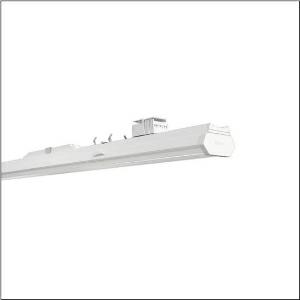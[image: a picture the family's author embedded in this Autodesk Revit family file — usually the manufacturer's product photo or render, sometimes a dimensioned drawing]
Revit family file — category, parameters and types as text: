
# Revit family: licross_r__11_protected_ho_51td11cn4exs_ee6c
name_source: partatom
category: Lighting Fixtures
units: mm (PartAtom-declared; Revit-internal decimal feet)

## family parameters
Cut with Voids When Loaded = No
Host = Face
Light Source = No
Part Type = Normal
Room Calculation Point = No
Round Connector Dimension = Use Diameter
Shared = No

## types (1)
- --- (1 x LED, 14460 lm, 77.6 W, 4000K)
    Apparent Load = 78 VA
    CIE Flux Codes = 84 94 98 99 100
    Color Rendering = 80
    Color Temperature = 4000K
    Default Elevation = 1800 mm
    Description = Licross® 11 Protected HO, luminaire insert, of sheet steel, galvanised, coil coated, white, length: 1.500mm, width: 90mm, height: 101mm, LED rated luminous flux: 14.460lm, light colour: 840, control gear: ON/OFF Multilumen, CLOi, with plug, 3-pole, with phase selection, mains connection: 220..240V, AC, 50/60Hz, start of lifetime: 78W, end of service life: 87W, internal wiring halogen-free, primary light control with lens, of plastic, primary optical cover: cover, of PMMA, light emission: direct distribution, primary light characteristic: symmetric, protection rating (complete): IP54, insulation class (complete): insulation class I (protective earthing), certification: CE, ENEC, VDE, UKCA, protection symbol: D if used in an environment with non-conductive dust loads with corresponding accessories, impact resistance: IK06, permissible ambient temperature for indoor applications: -35..+35°C, corresponds to IFS (International Featured Standards) requirements for safety and quality in the food industry, reducing of maximum allowable ambient temperature of 5°C with ceiling mounting, LABS conformity tested according to VDMA 24364:2018-05, packaging unit: 1 piece
    Height = 92 mm
    Lamp = 1 x LED
    Lamp Light Flux = 14460 lm
    Lamp Power = 77.6 W
    Lamp count = 1
    Length = 1500 mm
    Luminous efficacy = 186 lm/W
    Manufacturer = Siteco
    ModVariant = No
    Model = 51TD11CN4EXS
    Mounting Place = Ceiling
    Mounting Type = Pendant
    Number of Poles = 1
    OnlyDefault = Yes
    Power Factor = 1
    Product Name = Licross® 11 Protected HO
    Product group = luminaire insert | ceiling pendant
    ProductGroupID = 902
    Protection Class = Protection class I
    Protection Degree = IP 54
    RLX_Detail_Level = 1
    RLX_Emergency_Light_Flux = 0 lm
    RLX_Emergency_Type = 0
    RLX_Emergency_Type_DB = No
    RlxData = <blob elided: 22113 chars, md5=cae5a5b0>
    Socket = socket
    Standby Power = 0 W
    System Light Flux = 14460 lm
    System Power = 78 W
    Type Comments = factory setting: luminous flux: 100 % | (A | C | E) | 181 mA
    Type Image = l_1256145.jpg
    URL = http://relux.com
    VarID = @adj_107341
    Voltage = 0 V
    Weight = 0.00 kg
    Width = 88 mm

## geometry (parser evidence)
native form markers: Blend x4, Sweep x12
no freeform markers — native parametric forms only
